# Revit family: Washroom_Accessories-TSL-3002-Hand_Dryer-THESPLASHLAB-Slim
name_source: partatom
category: Specialty Equipment
revit_build: Autodesk Revit 2016 (Build: 20160314_0715(x64)
units: mm (PartAtom-declared; Revit-internal decimal feet)

## family parameters
Cut with Voids When Loaded = No
Host = Face
OmniClass Number = 23.40.20.21.14
OmniClass Title = Hand and Hair Dryers
Part Type = Normal
Room Calculation Point = No
Round Connector Dimension = Use Diameter
Shared = No

## types (1)
- TSL-3002_steel
    Assembly Code = E1010900
    AssetType = fixed
    Default Elevation = 1500 mm  [stored 4.92126 ft]
    DocumentationInstallationGuide = www.thesplashlab.com
    DocumentationLiterature = www.thesplashlab.com
    DocumentationMaintenance = www.thesplashlab.com
    DocumentationTechnical = www.thesplashlab.com
    DurationUnit = Years
    ExpectedLife = 3
    Finish = Brushed satin stainless steel
    Grade = 304
    Keynote = N13/360
    Manufacturer = TheSplashLab
    Material = Stainless Steel
    Model = TSL-3002
    Mtrl_ExpectedLife = 0
    Mtrl_Finish = Brushed satin stainless steel
    Mtrl_Grade = 304
    Mtrl_Material = Stainless Steel
    Mtrl_ReplacementCost = 0
    Mtrl_SerialNumber = 0
    Mtrl_TagNumber = 0
    Mtrl_WarrantyDurationLabor = 0
    Mtrl_WarrantyDurationParts = 0
    Mtrl_bimspec_guid = 0
    Mtrl_current revision = 0
    NBSObjectName = Washroom_Accessories-TSL-3002-Hand_Dryer-THESPLASHLAB-Slim
    NBSReference = 45-35-72/334
    Product Documentation Link = www.thesplashlab.com
    Product O&M Link = www.thesplashlab.com
    Product Page Link = www.thesplashlab.com
    Product Specification Link = www.thesplashlab.com
    Type Comments = Brushed satin stainless steel
    TypeName = TSL-3002
    URL = www.thesplashlab.com
    Uniclass2 = 45-35-72/334
    WarrantyDescription = 2 years from date of purchase
    WarrantyDurationParts = 3
    WarrantyDurationUnit = years
    _BIMspec_GUID = 0
    _current revision = 1
    material test = Brushed satin stainless steel

note: [stored X ft] marks values corroborated as IEEE doubles in the binary element streams (Revit-internal decimal feet)

## geometry (parser evidence)
native form markers: Blend x4, Sweep x2
no freeform markers — native parametric forms only
